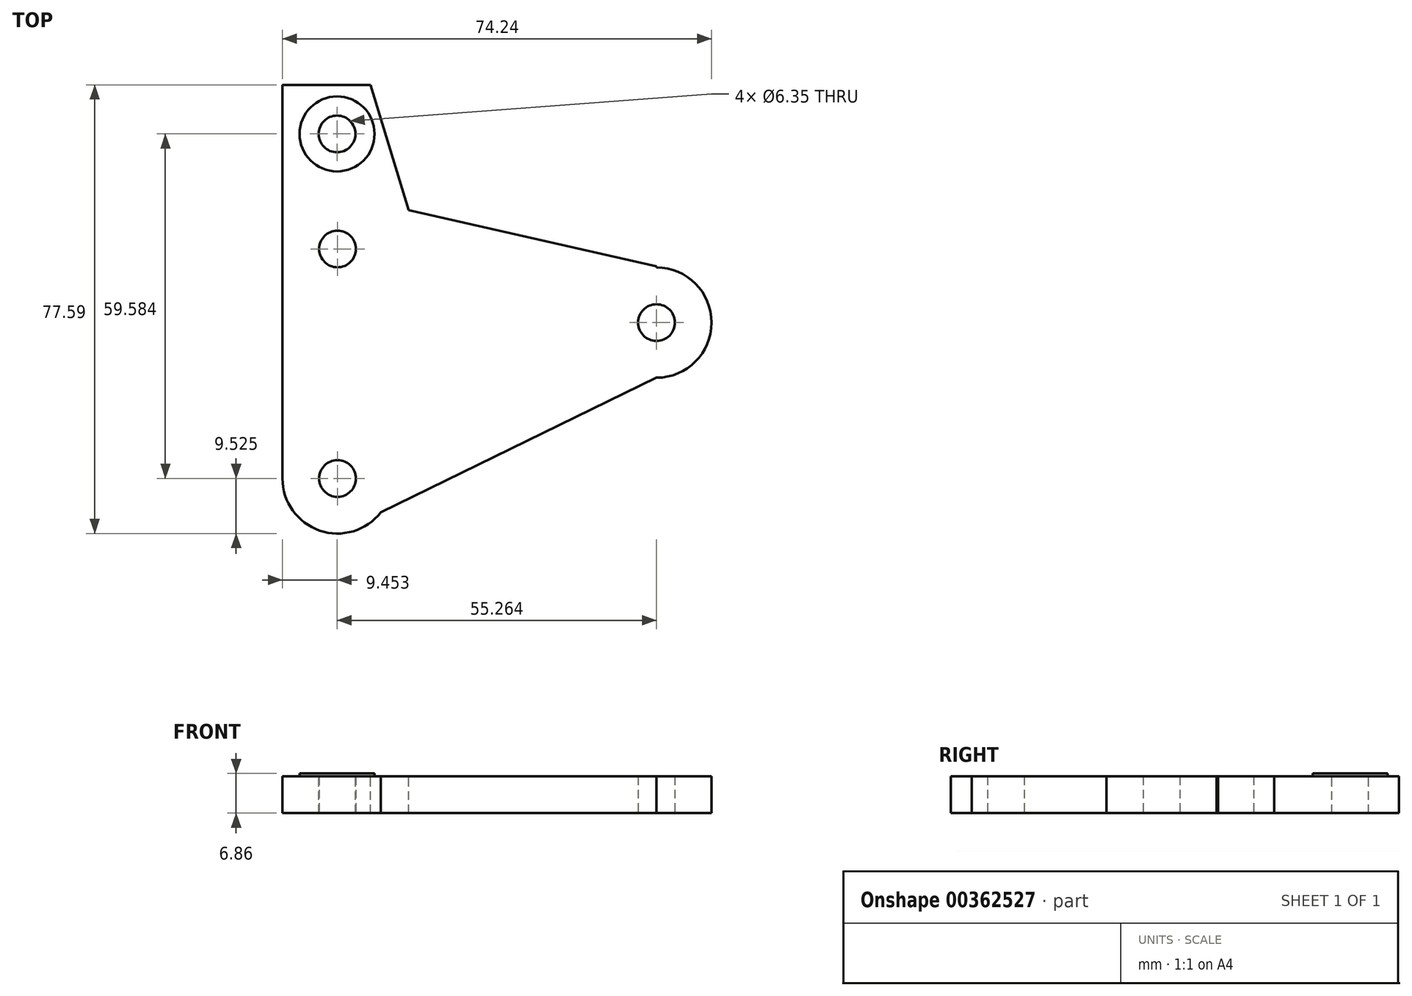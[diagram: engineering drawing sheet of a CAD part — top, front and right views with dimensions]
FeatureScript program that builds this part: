
annotation { "Feature Type Name" : "Feature", "Feature Type Description" : "" }
export const myFeature = defineFeature(function(context is Context, id is Id, definition is map)
    precondition{}
    {
        {
            var Q0;
            Q0=qCreatedBy(makeId("Top.planeOp"),FACE);
            var sketch = newSketch(context, id + "F0", { "sketchPlane" : qUnion([Q0])});
            skLineSegment(sketch, "E0", {"start": v(0, 0) * mm, "end": v(0, 12.74) * mm});
            skLineSegment(sketch, "E1", {"start": v(0, 0) * mm, "end": v(55.19, 0) * mm});
            skLineSegment(sketch, "E2", {"start": v(0, 0) * mm, "end": v(0, -26.96) * mm});
            skLineSegment(sketch, "E3", {"start": v(0, 12.74) * mm, "end": v(55.19, 0) * mm});
            skLineSegment(sketch, "E4", {"start": v(0, -26.96) * mm, "end": v(55.19, 0) * mm});
            skCircle(sketch, "E5", {"center": v(0, 12.74) * mm, "radius": 3.18 * mm});
            skCircle(sketch, "E6", {"center": v(55.19, 0) * mm, "radius": 3.18 * mm});
            skCircle(sketch, "E7", {"center": v(0, -26.96) * mm, "radius": 3.18 * mm});
            skCircle(sketch, "E8", {"center": v(0, -26.96) * mm, "radius": 9.53 * mm});
            skCircle(sketch, "E9", {"center": v(55.19, 0) * mm, "radius": 9.53 * mm});
            skCircle(sketch, "E10", {"center": v(0, 12.74) * mm, "radius": 9.53 * mm});
            skLineSegment(sketch, "E11", {"start": v(-9.53, 12.74) * mm, "end": v(-9.53, -26.96) * mm});
            skLineSegment(sketch, "E12", {"start": v(0, 12.74) * mm, "end": v(0, 22.27) * mm});
            skLineSegment(sketch, "E13", {"start": v(0, 22.27) * mm, "end": v(55.19, 9.77) * mm});
            skLineSegment(sketch, "E14", {"start": v(55.19, 9.77) * mm, "end": v(55.19, 0) * mm});
            skLineSegment(sketch, "E15", {"start": v(55.19, -9.52) * mm, "end": v(0, -36.48) * mm});
            skSolve(sketch);
        }
        {
            var Q0;
            Q0=qSketchRegion(id+"F0",true);
            var Q1;
            {var subQ3=sQuery(id+"F0.wireOp",EDGE,"E3");var subQ5=sQuery(id+"F0.wireOp",EDGE,"E10");var subQ6=makeQuery(id+"F0.imprint","INTERSECT",VERTEX,{"derivedFrom":[subQ3,subQ5]});Q1=makeQuery(id+"F0.imprint","IMPRINT",FACE,{"disambiguationData":[TD([[makeQuery(id+"F0.imprint","IMPRINT",EDGE,{"disambiguationData":[TD([[subQ6,-1.0]])],"derivedFrom":subQ3}),-1.0]])]});}
            var Q2;
            {var subQ0=sQuery(id+"F0.wireOp",EDGE,"E10");var subQ1=sQuery(id+"F0.wireOp",EDGE,"E0");var subQ2=makeQuery(id+"F0.imprint","INTERSECT",VERTEX,{"derivedFrom":[subQ1,subQ0]});Q2=makeQuery(id+"F0.imprint","IMPRINT",FACE,{"disambiguationData":[TD([[makeQuery(id+"F0.imprint","IMPRINT",EDGE,{"disambiguationData":[TD([[subQ2,-1.0]])],"derivedFrom":subQ1}),-1.0]])]});}
            var Q3;
            {var subQ0=sQuery(id+"F0.wireOp",EDGE,"E8");var subQ1=sQuery(id+"F0.wireOp",EDGE,"E4");var subQ2=makeQuery(id+"F0.imprint","INTERSECT",VERTEX,{"derivedFrom":[subQ1,subQ0]});Q3=makeQuery(id+"F0.imprint","IMPRINT",FACE,{"disambiguationData":[TD([[makeQuery(id+"F0.imprint","IMPRINT",EDGE,{"disambiguationData":[TD([[subQ2,-1.0]])],"derivedFrom":subQ1}),1.0]])]});}
            var Q4;
            {var subQ0=sQuery(id+"F0.wireOp",EDGE,"E8");var subQ1=sQuery(id+"F0.wireOp",EDGE,"E2");var subQ2=makeQuery(id+"F0.imprint","INTERSECT",VERTEX,{"derivedFrom":[subQ1,subQ0]});Q4=makeQuery(id+"F0.imprint","IMPRINT",FACE,{"disambiguationData":[TD([[makeQuery(id+"F0.imprint","IMPRINT",EDGE,{"disambiguationData":[TD([[subQ2,-1.0]])],"derivedFrom":subQ1}),1.0]])]});}
            var Q5;
            {var subQ0=sQuery(id+"F0.wireOp",EDGE,"E9");var subQ1=sQuery(id+"F0.wireOp",EDGE,"E1");var subQ2=makeQuery(id+"F0.imprint","INTERSECT",VERTEX,{"derivedFrom":[subQ1,subQ0]});Q5=makeQuery(id+"F0.imprint","IMPRINT",FACE,{"disambiguationData":[TD([[makeQuery(id+"F0.imprint","IMPRINT",EDGE,{"disambiguationData":[TD([[subQ2,-1.0]])],"derivedFrom":subQ1}),-1.0]])]});}
            var Q6;
            {var subQ0=sQuery(id+"F0.wireOp",EDGE,"E9");var subQ1=sQuery(id+"F0.wireOp",EDGE,"E1");var subQ2=makeQuery(id+"F0.imprint","INTERSECT",VERTEX,{"derivedFrom":[subQ1,subQ0]});Q6=makeQuery(id+"F0.imprint","IMPRINT",FACE,{"disambiguationData":[TD([[makeQuery(id+"F0.imprint","IMPRINT",EDGE,{"disambiguationData":[TD([[subQ2,-1.0]])],"derivedFrom":subQ1}),1.0]])]});}
            extrude(context, id + "F1", {"entities" : qUnion([Q0, Q1, Q2, Q3, Q4, Q5, Q6]), "depth" : 6.35 * mm});
        }
        {
            var Q0;
            Q0=makeQuery(id+"F1.opExtrude","CAP_FACE",FACE,{"disambiguationData":[OSD([sQuery(id+"F0.wireOp",EDGE,"E5"),sQuery(id+"F0.wireOp",EDGE,"E6"),sQuery(id+"F0.wireOp",EDGE,"E7"),sQuery(id+"F0.wireOp",EDGE,"E8"),sQuery(id+"F0.wireOp",EDGE,"E9"),sQuery(id+"F0.wireOp",EDGE,"E10"),sQuery(id+"F0.wireOp",EDGE,"E11"),sQuery(id+"F0.wireOp",EDGE,"E13"),sQuery(id+"F0.wireOp",EDGE,"E14"),sQuery(id+"F0.wireOp",EDGE,"E15")])],"isStart":false});
            var sketch = newSketch(context, id + "F2", { "sketchPlane" : qUnion([Q0])});
            skCircle(sketch, "E16", {"center": v(-0.08, 32.63) * mm, "radius": 3.18 * mm});
            skLineSegment(sketch, "E17", {"start": v(-9.53, 12.74) * mm, "end": v(-9.53, 41.11) * mm});
            skLineSegment(sketch, "E18", {"start": v(-9.53, 41.11) * mm, "end": v(5.72, 41.11) * mm});
            skLineSegment(sketch, "E19", {"start": v(5.72, 41.11) * mm, "end": v(12.32, 19.48) * mm});
            skLineSegment(sketch, "E20", {"start": v(12.32, 19.48) * mm, "end": v(-4.8, 16.78) * mm});
            skLineSegment(sketch, "E21", {"start": v(-4.8, 16.78) * mm, "end": v(-9.53, 12.74) * mm});
            skSolve(sketch);
        }
        {
            var Q0;
            Q0=makeQuery(id+"F2.imprint","IMPRINT",FACE,{"disambiguationData":[TD([[makeQuery(id+"F2.imprint","IMPRINT",EDGE,{"derivedFrom":sQuery(id+"F2.wireOp",EDGE,"E16")}),-1.0]])]});
            extrude(context, id + "F3", {"entities" : qUnion([Q0]), "operationType" : NewBodyOperationType.ADD, "oppositeDirection" : true, "depth" : 12.7 * mm});
        }
        {
            var Q0;
            Q0=makeQuery(id+"F3.opExtrude","CAP_FACE",FACE,{"disambiguationData":[OSD([sQuery(id+"F0.wireOp",EDGE,"E10"),sQuery(id+"F0.wireOp",EDGE,"E13"),sQuery(id+"F2.wireOp",EDGE,"E16"),sQuery(id+"F2.wireOp",EDGE,"E17"),sQuery(id+"F2.wireOp",EDGE,"E18"),sQuery(id+"F2.wireOp",EDGE,"E19")])],"isStart":false});
            var sketch = newSketch(context, id + "F4", { "sketchPlane" : qUnion([Q0])});
            skCircle(sketch, "E22", {"center": v(-0.08, -32.63) * mm, "radius": 6.48 * mm});
            skLineSegment(sketch, "E23", {"start": v(-22.7, -5.18) * mm, "end": v(28.05, -10.99) * mm});
            skLineSegment(sketch, "E24", {"start": v(28.05, -10.99) * mm, "end": v(22.35, -32.25) * mm});
            skLineSegment(sketch, "E25", {"start": v(22.35, -32.25) * mm, "end": v(-2.31, -53.08) * mm});
            skLineSegment(sketch, "E26", {"start": v(-2.31, -53.08) * mm, "end": v(-30.05, -35.98) * mm});
            skLineSegment(sketch, "E27", {"start": v(-30.05, -35.98) * mm, "end": v(-22.7, -5.18) * mm});
            skSolve(sketch);
        }
        {
            var Q0;
            Q0=makeQuery(id+"F4.imprint","IMPRINT",FACE,{"disambiguationData":[TD([[makeQuery(id+"F4.imprint","IMPRINT",EDGE,{"derivedFrom":sQuery(id+"F4.wireOp",EDGE,"E22")}),-1.0]])]});
            extrude(context, id + "F5", {"entities" : qUnion([Q0]), "operationType" : NewBodyOperationType.REMOVE, "oppositeDirection" : true, "depth" : 6.35 * mm});
        }
        {
            var Q0;
            Q0=makeQuery(id+"F3.opExtrude","CAP_FACE",FACE,{"disambiguationData":[OSD([sQuery(id+"F0.wireOp",EDGE,"E10"),sQuery(id+"F0.wireOp",EDGE,"E13"),sQuery(id+"F2.wireOp",EDGE,"E16"),sQuery(id+"F2.wireOp",EDGE,"E17"),sQuery(id+"F2.wireOp",EDGE,"E18"),sQuery(id+"F2.wireOp",EDGE,"E19")])],"isStart":false});
            extrude(context, id + "F6", {"entities" : qUnion([Q0]), "operationType" : NewBodyOperationType.ADD, "oppositeDirection" : true, "depth" : 19.56 * mm});
        }
        {
            var Q0;
            Q0=makeQuery(id+"F3.opExtrude","CAP_FACE",FACE,{"disambiguationData":[OSD([sQuery(id+"F0.wireOp",EDGE,"E10"),sQuery(id+"F0.wireOp",EDGE,"E13"),sQuery(id+"F2.wireOp",EDGE,"E16"),sQuery(id+"F2.wireOp",EDGE,"E17"),sQuery(id+"F2.wireOp",EDGE,"E18"),sQuery(id+"F2.wireOp",EDGE,"E19")])],"isStart":false});
            extrude(context, id + "F7", {"entities" : qUnion([Q0]), "operationType" : NewBodyOperationType.REMOVE, "oppositeDirection" : true, "depth" : 6.35 * mm});
        }
        {
            var Q0;
            Q0=makeQuery(id+"F6.opExtrude","CAP_FACE",FACE,{"disambiguationData":[OSD([sQuery(id+"F0.wireOp",EDGE,"E10"),sQuery(id+"F0.wireOp",EDGE,"E13"),sQuery(id+"F2.wireOp",EDGE,"E16"),sQuery(id+"F2.wireOp",EDGE,"E17"),sQuery(id+"F2.wireOp",EDGE,"E18"),sQuery(id+"F2.wireOp",EDGE,"E19")])],"isStart":false});
            var sketch = newSketch(context, id + "F8", { "sketchPlane" : qUnion([Q0])});
            skSolve(sketch);
        }
        {
            var Q0;
            Q0 = qSketchRegion(id + "F8", true);
            var Q1;
            Q1=makeQuery(id+"F8.imprint","IMPRINT",FACE,{"disambiguationData":[TD([[makeQuery(id+"F8.imprint","IMPRINT",EDGE,{"derivedFrom":makeQuery(id+"F6.opExtrude","CAP_EDGE",EDGE,{"disambiguationData":[OSD([sQuery(id+"F2.wireOp",EDGE,"E16")])],"isStart":false})}),-1.0]])]});
            extrude(context, id + "F9", {"entities" : qUnion([Q0, Q1]), "operationType" : NewBodyOperationType.REMOVE, "oppositeDirection" : true, "depth" : 6.35 * mm});
        }
    });
